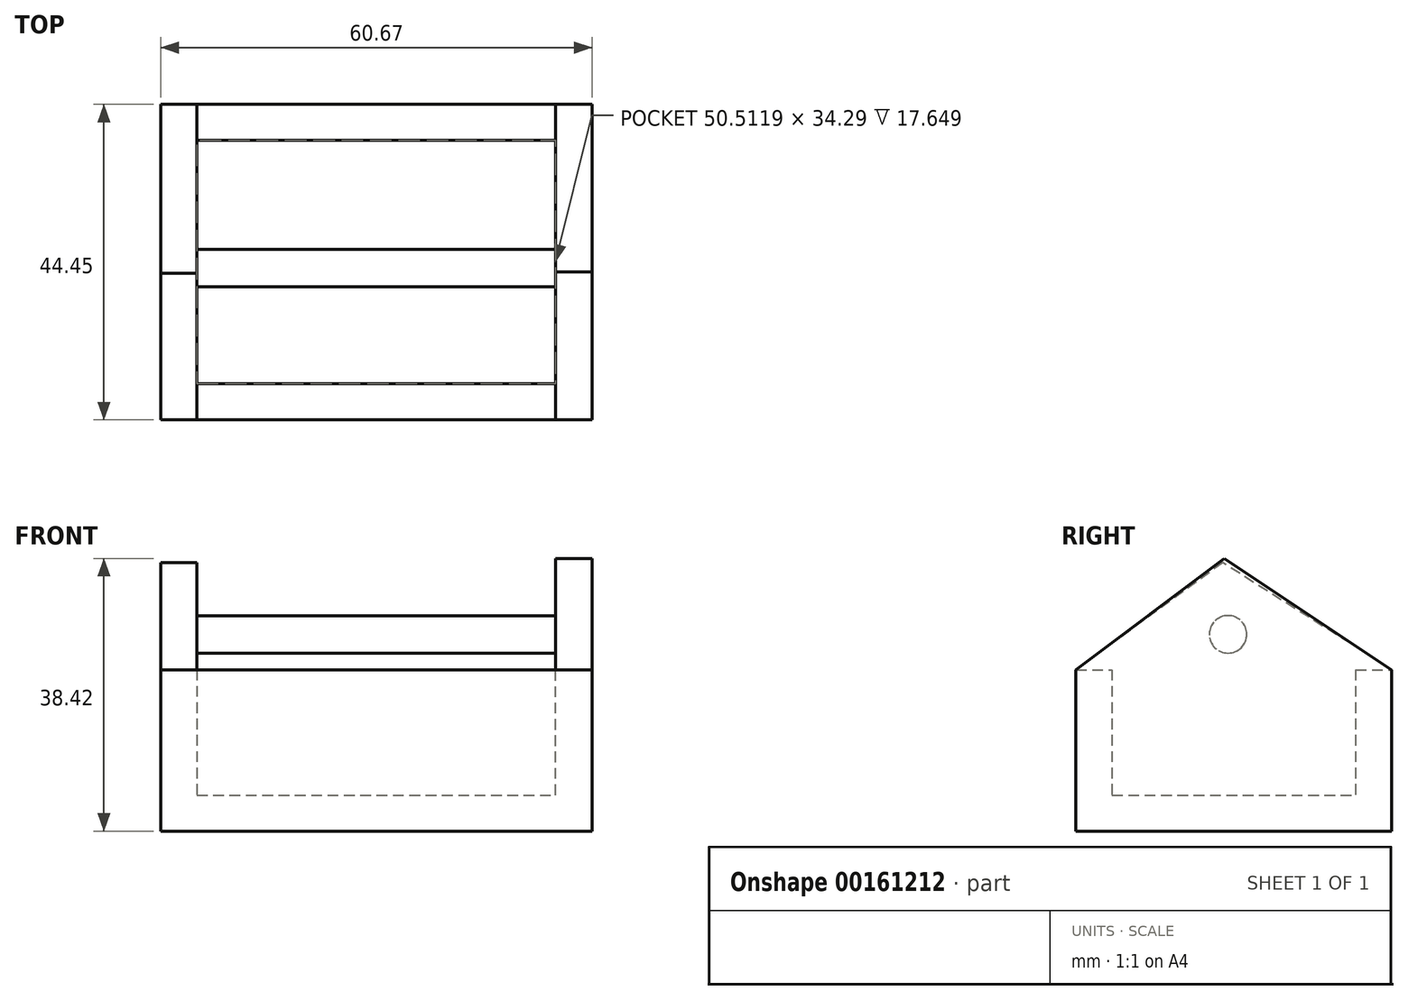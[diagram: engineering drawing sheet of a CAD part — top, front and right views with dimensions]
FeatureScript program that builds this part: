
annotation { "Feature Type Name" : "Feature", "Feature Type Description" : "" }
export const myFeature = defineFeature(function(context is Context, id is Id, definition is map)
    precondition{}
    {
        {
            var Q0;
            Q0=qCreatedBy(makeId("Front.planeOp"),FACE);
            var sketch = newSketch(context, id + "F0", { "sketchPlane" : qUnion([Q0])});
            skLineSegment(sketch, "E0", {"start": v(-30.8, 11.27) * mm, "end": v(-30.8, -11.46) * mm});
            skLineSegment(sketch, "E1", {"start": v(-30.8, -11.46) * mm, "end": v(29.88, -11.46) * mm});
            skLineSegment(sketch, "E2", {"start": v(29.88, -11.46) * mm, "end": v(29.88, 11.82) * mm});
            skLineSegment(sketch, "E3", {"start": v(-30.8, 11.27) * mm, "end": v(29.88, 11.27) * mm});
            skSolve(sketch);
        }
        {
            var Q0;
            Q0=makeQuery(id+"F0.imprint","IMPRINT",FACE,{"disambiguationData":[TD([[makeQuery(id+"F0.imprint","IMPRINT",EDGE,{"derivedFrom":sQuery(id+"F0.wireOp",EDGE,"E0")}),1.0]])]});
            extrude(context, id + "F1", {"entities" : qUnion([Q0]), "depth" : 44.45 * mm});
        }
        {
            var Q0;
            Q0=makeQuery(id+"F1.opExtrude","SWEPT_FACE",FACE,{"disambiguationData":[OSD([sQuery(id+"F0.wireOp",EDGE,"E3")])]});
            shell(context, id + "F2", {"entities" : qUnion([Q0]), "thickness" : 5.08 * mm});
        }
        {
            var Q0;
            Q0=makeQuery(id+"F1.opExtrude","SWEPT_FACE",FACE,{"disambiguationData":[OSD([sQuery(id+"F0.wireOp",EDGE,"E2")])]});
            var sketch = newSketch(context, id + "F3", { "sketchPlane" : qUnion([Q0])});
            skLineSegment(sketch, "E4", {"start": v(-44.45, 11.27) * mm, "end": v(-23.58, 26.96) * mm});
            skLineSegment(sketch, "E5", {"start": v(-23.58, 26.96) * mm, "end": v(0, 11.27) * mm});
            skSolve(sketch);
        }
        {
            var Q0;
            Q0=makeQuery(id+"F3.imprint","IMPRINT",FACE,{"disambiguationData":[TD([[makeQuery(id+"F3.imprint","IMPRINT",EDGE,{"derivedFrom":sQuery(id+"F3.wireOp",EDGE,"E4")}),-1.0]])]});
            extrude(context, id + "F4", {"entities" : qUnion([Q0]), "operationType" : NewBodyOperationType.ADD, "oppositeDirection" : true, "depth" : 5.08 * mm});
        }
        {
            var Q0;
            Q0=makeQuery(id+"F1.opExtrude","SWEPT_FACE",FACE,{"disambiguationData":[OSD([sQuery(id+"F0.wireOp",EDGE,"E0")])]});
            var sketch = newSketch(context, id + "F5", { "sketchPlane" : qUnion([Q0])});
            skLineSegment(sketch, "E6", {"start": v(0, 11.27) * mm, "end": v(23.8, 26.34) * mm});
            skLineSegment(sketch, "E7", {"start": v(23.8, 26.34) * mm, "end": v(44.45, 11.27) * mm});
            skSolve(sketch);
        }
        {
            var Q0;
            Q0=makeQuery(id+"F5.imprint","IMPRINT",FACE,{"disambiguationData":[TD([[makeQuery(id+"F5.imprint","IMPRINT",EDGE,{"derivedFrom":sQuery(id+"F5.wireOp",EDGE,"E6")}),-1.0]])]});
            extrude(context, id + "F6", {"entities" : qUnion([Q0]), "operationType" : NewBodyOperationType.ADD, "oppositeDirection" : true, "depth" : 5.08 * mm});
        }
        {
            var Q0;
            {var subQ0=sQuery(id+"F0.wireOp",EDGE,"E0");Q0=makeQuery(id+"F6.boolean.opBoolean","MERGE",FACE,{"derivedFrom":[makeQuery(id+"F2.opShell","OFFSET_FACE",FACE,{"disambiguationData":[OSD([subQ0])]}),makeQuery(id+"F6.opExtrude","CAP_FACE",FACE,{"disambiguationData":[OSD([subQ0,sQuery(id+"F0.wireOp",EDGE,"E3"),sQuery(id+"F5.wireOp",EDGE,"E6"),sQuery(id+"F5.wireOp",EDGE,"E7")])],"isStart":false})]});}
            var sketch = newSketch(context, id + "F7", { "sketchPlane" : qUnion([Q0])});
            skCircle(sketch, "E8", {"center": v(-23.05, 16.25) * mm, "radius": 2.64 * mm});
            skSolve(sketch);
        }
        {
            var Q0;
            Q0=makeQuery(id+"F7.imprint","IMPRINT",FACE,{"disambiguationData":[TD([[makeQuery(id+"F7.imprint","IMPRINT",EDGE,{"derivedFrom":sQuery(id+"F7.wireOp",EDGE,"E8")}),1.0]])]});
            extrude(context, id + "F8", {"entities" : qUnion([Q0]), "operationType" : NewBodyOperationType.ADD, "depth" : 55.24 * mm});
        }
    });
